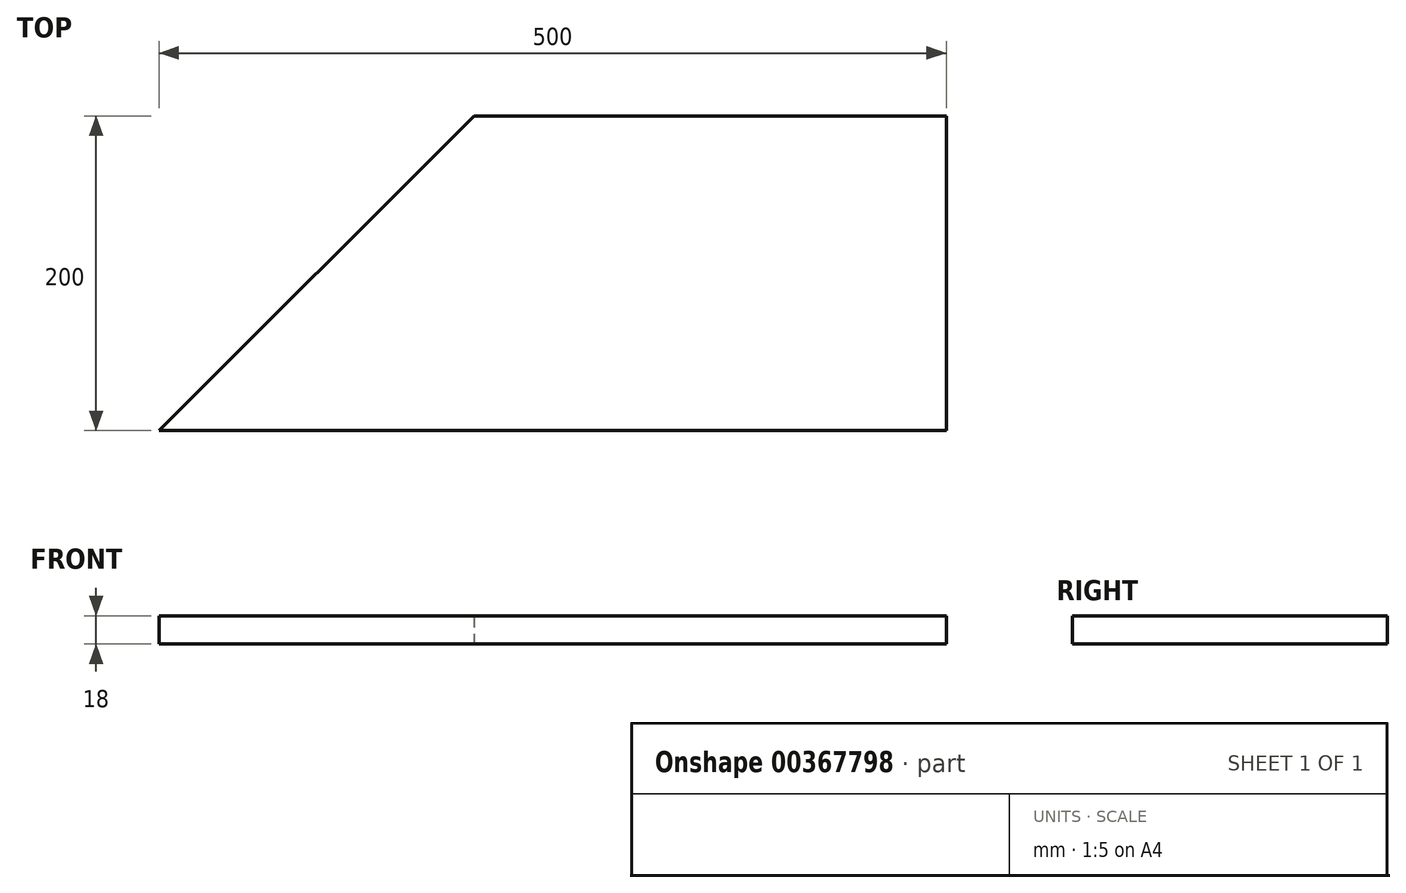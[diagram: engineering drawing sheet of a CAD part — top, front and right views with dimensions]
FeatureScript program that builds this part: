
annotation { "Feature Type Name" : "Feature", "Feature Type Description" : "" }
export const myFeature = defineFeature(function(context is Context, id is Id, definition is map)
    precondition{}
    {
        {
            var Q0;
            Q0=qCreatedBy(makeId("Top.planeOp"),FACE);
            var sketch = newSketch(context, id + "F0", { "sketchPlane" : qUnion([Q0])});
            skLineSegment(sketch, "E0", {"start": v(0, 0) * mm, "end": v(500, 0) * mm});
            skLineSegment(sketch, "E1", {"start": v(200, 200) * mm, "end": v(0, 0) * mm});
            skLineSegment(sketch, "E2", {"start": v(500, 200) * mm, "end": v(200, 200) * mm});
            skLineSegment(sketch, "E3", {"start": v(500, 0) * mm, "end": v(500, 200) * mm});
            skSolve(sketch);
        }
        {
            var Q0;
            Q0=makeQuery(id+"F0.imprint","IMPRINT",FACE,{"disambiguationData":[TD([[makeQuery(id+"F0.imprint","IMPRINT",EDGE,{"derivedFrom":sQuery(id+"F0.wireOp",EDGE,"E0")}),1.0]])]});
            extrude(context, id + "F1", {"entities" : qUnion([Q0]), "depth" : 18 * mm});
        }
    });
